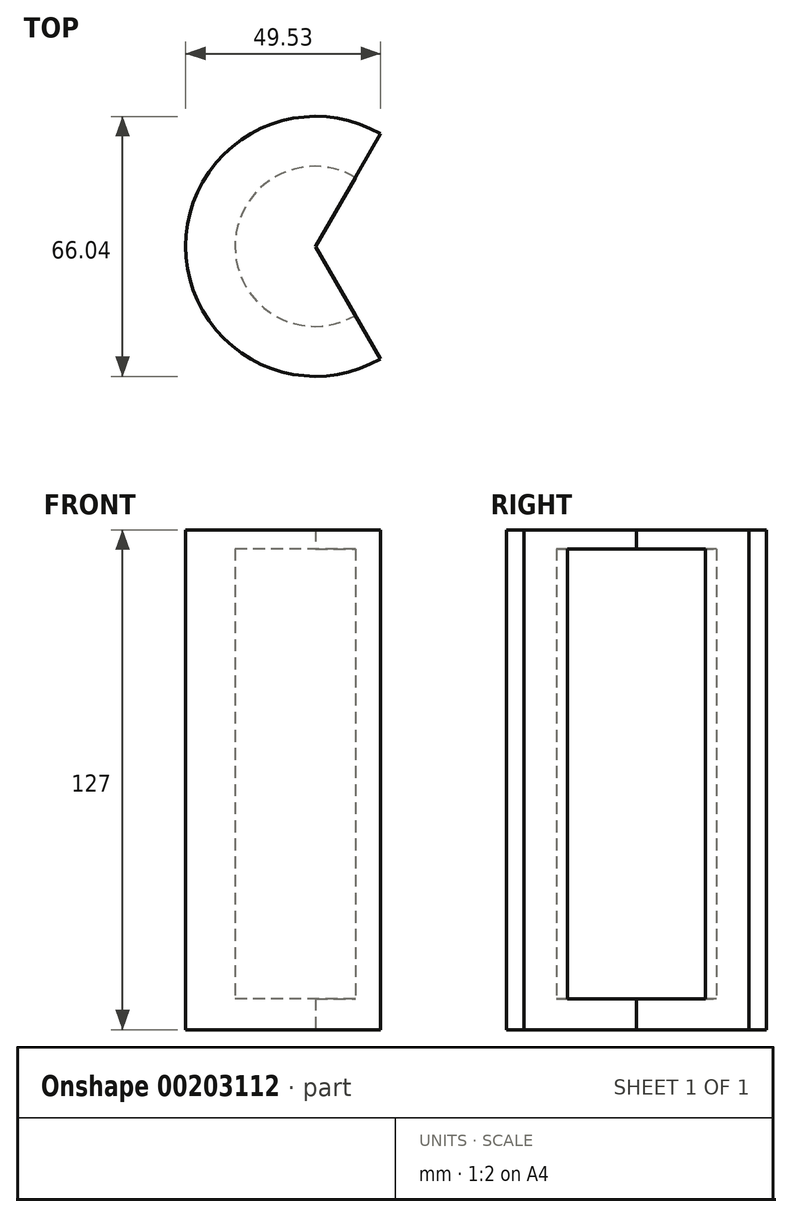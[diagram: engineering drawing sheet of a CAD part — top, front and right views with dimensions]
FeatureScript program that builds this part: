
annotation { "Feature Type Name" : "Feature", "Feature Type Description" : "" }
export const myFeature = defineFeature(function(context is Context, id is Id, definition is map)
    precondition{}
    {
        {
            var Q0;
            Q0=qCreatedBy(makeId("Front.planeOp"),FACE);
            var sketch = newSketch(context, id + "F0", { "sketchPlane" : qUnion([Q0])});
            skLineSegment(sketch, "E0.bottom", {"start": v(-33.23, 51.56) * mm, "end": v(-0.21, 51.56) * mm});
            skLineSegment(sketch, "E0.top", {"start": v(-33.23, -75.44) * mm, "end": v(-0.21, -75.44) * mm});
            skLineSegment(sketch, "E0.left", {"start": v(-33.23, 51.56) * mm, "end": v(-33.23, -75.44) * mm});
            skLineSegment(sketch, "E0.right", {"start": v(-0.21, 51.56) * mm, "end": v(-0.21, -75.44) * mm});
            skSolve(sketch);
        }
        {
            var Q0;
            Q0 = qSketchRegion(id + "F0", true);
            var Q1;
            Q1=sQuery(id+"F0.wireOp",EDGE,"E0.right");
            revolve(context, id + "F1", {"entities" : qUnion([Q0]), "axis" : qUnion([Q1]), "revolveType" : RevolveType.SYMMETRIC, "angle" : 240 * degree});
        }
        {
            var Q0;
            Q0=qCreatedBy(makeId("Front.planeOp"),FACE);
            var sketch = newSketch(context, id + "F2", { "sketchPlane" : qUnion([Q0])});
            skLineSegment(sketch, "E1.bottom", {"start": v(-20.7, 46.73) * mm, "end": v(-0.37, 46.73) * mm});
            skLineSegment(sketch, "E1.top", {"start": v(-20.7, -67.57) * mm, "end": v(-0.37, -67.57) * mm});
            skLineSegment(sketch, "E1.left", {"start": v(-20.7, 46.73) * mm, "end": v(-20.7, -67.57) * mm});
            skLineSegment(sketch, "E1.right", {"start": v(-0.37, 46.73) * mm, "end": v(-0.37, -67.57) * mm});
            skSolve(sketch);
        }
        {
            var Q0;
            Q0 = qSketchRegion(id + "F2", true);
            var Q1;
            Q1=sQuery(id+"F2.wireOp",EDGE,"E1.right");
            revolve(context, id + "F3", {"operationType" : NewBodyOperationType.REMOVE, "entities" : qUnion([Q0]), "axis" : qUnion([Q1]), "revolveType" : RevolveType.FULL, "oppositeDirection" : true});
        }
    });
